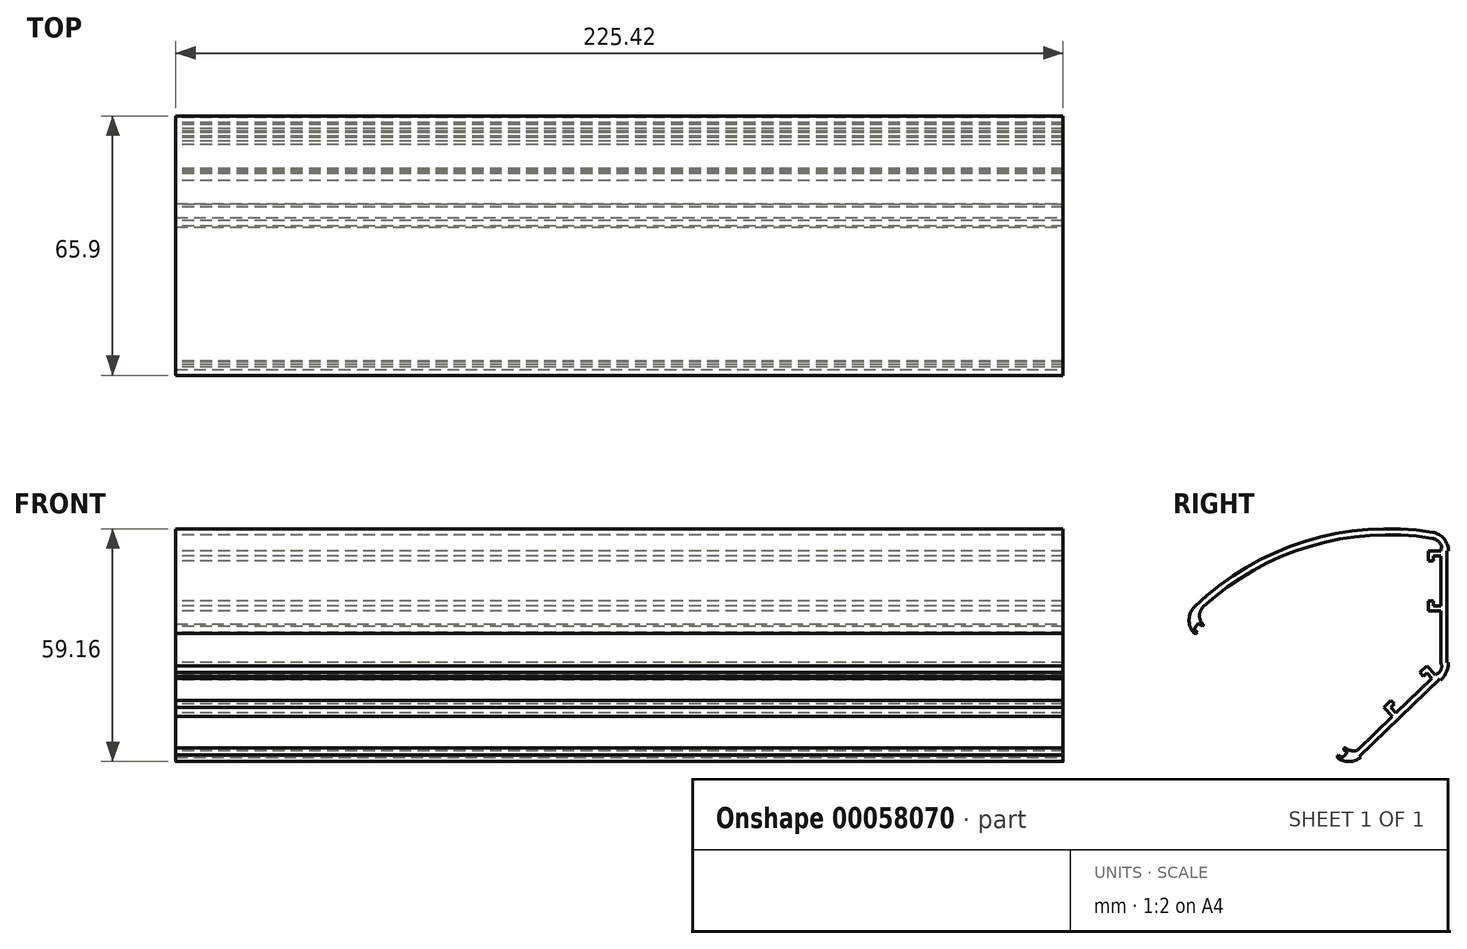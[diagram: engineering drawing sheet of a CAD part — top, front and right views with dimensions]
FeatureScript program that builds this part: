
annotation { "Feature Type Name" : "Feature", "Feature Type Description" : "" }
export const myFeature = defineFeature(function(context is Context, id is Id, definition is map)
    precondition{}
    {
        {
            var Q0;
            Q0=qCreatedBy(makeId("Right.planeOp"),FACE);
            var sketch = newSketch(context, id + "F0", { "sketchPlane" : qUnion([Q0])});
            skLineSegment(sketch, "E0", {"start": v(-25.12, -24.26) * mm, "end": v(0, 0) * mm});
            skLineSegment(sketch, "E1", {"start": v(0, 0) * mm, "end": v(0, 34.93) * mm});
            skArc(sketch, "E2", {"start": v(0, 34.92) * mm, "mid": v(-34.7, 33.87) * mm, "end": v(-64.76, 16.49) * mm});
            skLineSegment(sketch, "E3", {"start": v(-64.76, 16.49) * mm, "end": v(-68.18, 13.16) * mm});
            skLineSegment(sketch, "E4", {"start": v(-25.12, -24.26) * mm, "end": v(-68.18, 13.16) * mm});
            skLineSegment(sketch, "E5", {"start": v(-64.76, 16.49) * mm, "end": v(-25.12, -24.26) * mm, "construction": true});
            skLineSegment(sketch, "E6", {"start": v(-64.76, 16.49) * mm, "end": v(0, 34.93) * mm, "construction": true});
            skSolve(sketch);
        }
        {
            var Q0;
            Q0=qSketchRegion(id+"F0",true);
            extrude(context, id + "F1", {"entities" : qUnion([Q0]), "endBound" : BoundingType.SYMMETRIC, "depth" : 225.42 * mm});
        }
        {
            var Q0;
            Q0=makeQuery(id+"F1.opExtrude","SWEPT_EDGE",EDGE,{"disambiguationData":[OSD([sQuery(id+"F0.wireOp",EDGE,"E1"),sQuery(id+"F0.wireOp",EDGE,"E2")])]});
            var Q1;
            Q1=makeQuery(id+"F1.opExtrude","SWEPT_EDGE",EDGE,{"disambiguationData":[OSD([sQuery(id+"F0.wireOp",EDGE,"E0"),sQuery(id+"F0.wireOp",EDGE,"E4")])]});
            var Q2;
            Q2=makeQuery(id+"F1.opExtrude","SWEPT_EDGE",EDGE,{"disambiguationData":[OSD([sQuery(id+"F0.wireOp",EDGE,"E3"),sQuery(id+"F0.wireOp",EDGE,"E4")])]});
            fillet(context, id + "F2", {"entities" : qUnion([Q0, Q1, Q2]), "radius" : 4.76 * mm, "tangentPropagation" : true, "allowEdgeOverflow" : false});
        }
        {
            var Q0;
            Q0=makeQuery(id+"F1.opExtrude","SWEPT_EDGE",EDGE,{"disambiguationData":[OSD([sQuery(id+"F0.wireOp",EDGE,"E0"),sQuery(id+"F0.wireOp",EDGE,"E1")])]});
            fillet(context, id + "F3", {"entities" : qUnion([Q0]), "radius" : 6.35 * mm, "tangentPropagation" : true, "allowEdgeOverflow" : false});
        }
        {
            var Q0;
            Q0=makeQuery(id+"F1.opExtrude","CAP_FACE",FACE,{"disambiguationData":[OSD([sQuery(id+"F0.wireOp",EDGE,"E0"),sQuery(id+"F0.wireOp",EDGE,"E1"),sQuery(id+"F0.wireOp",EDGE,"E2"),sQuery(id+"F0.wireOp",EDGE,"E3"),sQuery(id+"F0.wireOp",EDGE,"E4")])],"isStart":true});
            var Q1;
            Q1=makeQuery(id+"F1.opExtrude","CAP_FACE",FACE,{"disambiguationData":[OSD([sQuery(id+"F0.wireOp",EDGE,"E0"),sQuery(id+"F0.wireOp",EDGE,"E1"),sQuery(id+"F0.wireOp",EDGE,"E2"),sQuery(id+"F0.wireOp",EDGE,"E3"),sQuery(id+"F0.wireOp",EDGE,"E4")])],"isStart":false});
            var Q2;
            Q2=makeQuery(id+"F1.opExtrude","SWEPT_FACE",FACE,{"disambiguationData":[OSD([sQuery(id+"F0.wireOp",EDGE,"E4")])]});
            shell(context, id + "F4", {"entities" : qUnion([Q0, Q1, Q2]), "thickness" : 1.52 * mm});
        }
        {
            var Q0;
            Q0=makeQuery(id+"F1.opExtrude","CAP_FACE",FACE,{"disambiguationData":[OSD([sQuery(id+"F0.wireOp",EDGE,"E0"),sQuery(id+"F0.wireOp",EDGE,"E1"),sQuery(id+"F0.wireOp",EDGE,"E2"),sQuery(id+"F0.wireOp",EDGE,"E3"),sQuery(id+"F0.wireOp",EDGE,"E4")])],"isStart":true});
            var sketch = newSketch(context, id + "F5", { "sketchPlane" : qUnion([Q0])});
            skLineSegment(sketch, "E7", {"start": v(63.27, 10.92) * mm, "end": v(62.18, 12.16) * mm});
            skArc(sketch, "E8.0", {"start": v(63.27, 10.92) * mm, "mid": v(64.38, 13.28) * mm, "end": v(63.39, 15.7) * mm});
            skArc(sketch, "E9", {"start": v(62.18, 12.16) * mm, "mid": v(63.23, 14.47) * mm, "end": v(62.22, 16.8) * mm});
            skSolve(sketch);
        }
        {
            var Q0;
            {var subQ0=sQuery(id+"F0.wireOp",EDGE,"E3");Q0=makeQuery(id+"FXWxfeTe23RxrKB_1.boolean.opBoolean","MERGE",FACE,{"derivedFrom":[makeQuery(id+"F1.opExtrude","CAP_FACE",FACE,{"disambiguationData":[OSD([sQuery(id+"F0.wireOp",EDGE,"E0"),sQuery(id+"F0.wireOp",EDGE,"E1"),sQuery(id+"F0.wireOp",EDGE,"E2"),subQ0,sQuery(id+"F0.wireOp",EDGE,"E4")])],"isStart":true}),makeQuery(id+"FXWxfeTe23RxrKB_1.opExtrude","CAP_FACE",FACE,{"disambiguationData":[OSD([subQ0,sQuery(id+"F5.wireOp",EDGE,"f8929549-29da-4568-b1ae-587f62ae2228.0"),sQuery(id+"F5.wireOp",EDGE,"E7"),sQuery(id+"F5.wireOp",EDGE,"b0cd2a88-d953-423b-8e6f-4eb86873c5e2")])],"isStart":true})]});}
            var sketch = newSketch(context, id + "F6", { "sketchPlane" : qUnion([Q0])});
            skArc(sketch, "E10.0", {"start": v(23.04, -20.13) * mm, "mid": v(25.2, -21.04) * mm, "end": v(27.42, -20.25) * mm});
            skLineSegment(sketch, "E11", {"start": v(27.42, -20.25) * mm, "end": v(26.33, -19) * mm});
            skArc(sketch, "E12", {"start": v(21.75, -18.88) * mm, "mid": v(24.02, -19.83) * mm, "end": v(26.33, -19) * mm});
            skLineSegment(sketch, "E13", {"start": v(26.33, -19) * mm, "end": v(24.2, -20.85) * mm, "construction": true});
            skSolve(sketch);
        }
        {
            var Q0;
            Q0=makeQuery(id+"F5.imprint","IMPRINT",FACE,{"disambiguationData":[TD([[makeQuery(id+"F5.imprint","IMPRINT",EDGE,{"derivedFrom":sQuery(id+"F5.wireOp",EDGE,"E7")}),-1.0]])]});
            var Q1;
            {var subQ0=sQuery(id+"F6.wireOp",EDGE,"E10.0");Q1=makeQuery(id+"F6.imprint","IMPRINT",FACE,{"disambiguationData":[TD([[makeQuery(id+"F6.imprint","IMPRINT",EDGE,{"derivedFrom":subQ0}),1.0]])]});}
            var Q2;
            Q2=makeQuery(id+"F1.opExtrude","CAP_FACE",FACE,{"disambiguationData":[OSD([sQuery(id+"F0.wireOp",EDGE,"E0"),sQuery(id+"F0.wireOp",EDGE,"E1"),sQuery(id+"F0.wireOp",EDGE,"E2"),sQuery(id+"F0.wireOp",EDGE,"E3"),sQuery(id+"F0.wireOp",EDGE,"E4")])],"isStart":false});
            extrude(context, id + "F7", {"entities" : qUnion([Q0, Q1]), "operationType" : NewBodyOperationType.ADD, "endBound" : BoundingType.UP_TO_SURFACE, "oppositeDirection" : true, "endBoundEntityFace" : qUnion([Q2]), "depth" : 25.4 * mm});
        }
        {
            var Q0;
            {var subQ0=sQuery(id+"F0.wireOp",EDGE,"E0");var subQ1=sQuery(id+"F0.wireOp",EDGE,"E2");Q0=makeQuery(id+"F7.boolean.opBoolean","MERGE",FACE,{"derivedFrom":[makeQuery(id+"F1.opExtrude","CAP_FACE",FACE,{"disambiguationData":[OSD([subQ0,sQuery(id+"F0.wireOp",EDGE,"E1"),subQ1,sQuery(id+"F0.wireOp",EDGE,"E3"),sQuery(id+"F0.wireOp",EDGE,"E4")])],"isStart":true}),makeQuery(id+"F7.opExtrude","CAP_FACE",FACE,{"disambiguationData":[OSD([subQ1,sQuery(id+"F5.wireOp",EDGE,"E7"),sQuery(id+"F5.wireOp",EDGE,"E8.0"),sQuery(id+"F5.wireOp",EDGE,"E9")])],"isStart":true}),makeQuery(id+"F7.opExtrude","CAP_FACE",FACE,{"disambiguationData":[OSD([subQ0,sQuery(id+"F6.wireOp",EDGE,"E10.0"),sQuery(id+"F6.wireOp",EDGE,"E11"),sQuery(id+"F6.wireOp",EDGE,"E12")])],"isStart":true})]});}
            var sketch = newSketch(context, id + "F8", { "sketchPlane" : qUnion([Q0])});
            skLineSegment(sketch, "E14", {"start": v(63.18, 11.01) * mm, "end": v(27.33, -20.15) * mm, "construction": true});
            skSolve(sketch);
        }
        {
            var Q0;
            {var subQ4=sQuery(id+"F0.wireOp",EDGE,"E0");var subQ12=makeQuery(id+"F1.opExtrude","CAP_EDGE",EDGE,{"disambiguationData":[OSD([subQ4])],"isStart":true});Q0=makeQuery(id+"F8.imprint","IMPRINT",FACE,{"disambiguationData":[TD([[makeQuery(id+"F8.imprint","IMPRINT",EDGE,{"derivedFrom":subQ12}),-1.0]])]});}
            var sketch = newSketch(context, id + "F9", { "sketchPlane" : qUnion([Q0])});
            skLineSegment(sketch, "E15", {"start": v(62.56, 11.73) * mm, "end": v(63.8, 10.3) * mm});
            skLineSegment(sketch, "E16", {"start": v(63.8, 10.3) * mm, "end": v(64.77, 11.13) * mm});
            skLineSegment(sketch, "E17", {"start": v(64.77, 11.13) * mm, "end": v(63.52, 12.56) * mm});
            skLineSegment(sketch, "E18", {"start": v(63.52, 12.56) * mm, "end": v(62.56, 11.73) * mm});
            skPoint(sketch, "E19", {"position": v(63.18, 11.01) * mm});
            skSolve(sketch);
        }
        {
            var Q0;
            {var subQ4=sQuery(id+"F0.wireOp",EDGE,"E0");var subQ12=makeQuery(id+"F1.opExtrude","CAP_EDGE",EDGE,{"disambiguationData":[OSD([subQ4])],"isStart":true});Q0=makeQuery(id+"F8.imprint","IMPRINT",FACE,{"disambiguationData":[TD([[makeQuery(id+"F8.imprint","IMPRINT",EDGE,{"derivedFrom":subQ12}),-1.0]])]});}
            var sketch = newSketch(context, id + "F10", { "sketchPlane" : qUnion([Q0])});
            skLineSegment(sketch, "E20", {"start": v(26.7, -19.43) * mm, "end": v(27.96, -20.87) * mm});
            skLineSegment(sketch, "E21", {"start": v(27.96, -20.87) * mm, "end": v(27, -21.7) * mm});
            skLineSegment(sketch, "E22", {"start": v(27, -21.7) * mm, "end": v(25.75, -20.27) * mm});
            skLineSegment(sketch, "E23", {"start": v(25.75, -20.27) * mm, "end": v(26.7, -19.43) * mm});
            skPoint(sketch, "E24", {"position": v(27.33, -20.15) * mm});
            skSolve(sketch);
        }
        {
            var Q0;
            Q0=qSketchRegion(id+"F9",true);
            var Q1;
            Q1=qSketchRegion(id+"F10",true);
            var Q2;
            {var subQ0=sQuery(id+"F0.wireOp",EDGE,"E0");var subQ1=sQuery(id+"F0.wireOp",EDGE,"E2");Q2=makeQuery(id+"F7.boolean.opBoolean","MERGE",FACE,{"derivedFrom":[makeQuery(id+"F1.opExtrude","CAP_FACE",FACE,{"disambiguationData":[OSD([subQ0,sQuery(id+"F0.wireOp",EDGE,"E1"),subQ1,sQuery(id+"F0.wireOp",EDGE,"E3"),sQuery(id+"F0.wireOp",EDGE,"E4")])],"isStart":false}),makeQuery(id+"F7.opExtrude","CAP_FACE",FACE,{"disambiguationData":[OSD([subQ1,sQuery(id+"F5.wireOp",EDGE,"E7"),sQuery(id+"F5.wireOp",EDGE,"E8.0"),sQuery(id+"F5.wireOp",EDGE,"E9")])],"isStart":false}),makeQuery(id+"F7.opExtrude","CAP_FACE",FACE,{"disambiguationData":[OSD([subQ0,sQuery(id+"F6.wireOp",EDGE,"E10.0"),sQuery(id+"F6.wireOp",EDGE,"E11"),sQuery(id+"F6.wireOp",EDGE,"E12")])],"isStart":false})]});}
            extrude(context, id + "F11", {"entities" : qUnion([Q0, Q1]), "operationType" : NewBodyOperationType.REMOVE, "endBound" : BoundingType.UP_TO_SURFACE, "oppositeDirection" : true, "endBoundEntityFace" : qUnion([Q2]), "depth" : 25.4 * mm});
        }
        {
            var Q0;
            Q0=makeQuery(id+"F11.boolean.opBoolean","COPY",EDGE,{"derivedFrom":makeQuery(id+"F11.opExtrude","SWEPT_EDGE",EDGE,{"disambiguationData":[OSD([sQuery(id+"F10.wireOp",EDGE,"E21"),sQuery(id+"F10.wireOp",EDGE,"E22")])]})});
            var Q1;
            Q1=makeQuery(id+"F11.boolean.opBoolean","COPY",EDGE,{"derivedFrom":makeQuery(id+"F11.opExtrude","SWEPT_EDGE",EDGE,{"disambiguationData":[OSD([sQuery(id+"F9.wireOp",EDGE,"E16"),sQuery(id+"F9.wireOp",EDGE,"E17")])]})});
            fillet(context, id + "F12", {"entities" : qUnion([Q0, Q1]), "radius" : 0.76 * mm, "tangentPropagation" : true, "allowEdgeOverflow" : false});
        }
        {
            var Q0;
            {var subQ0=sQuery(id+"F0.wireOp",EDGE,"E4");Q0=makeQuery(id+"F2.opFillet","BLEND_EDGE",EDGE,{"blendedFrom":[makeQuery(id+"F1.opExtrude","SWEPT_EDGE",EDGE,{"disambiguationData":[OSD([sQuery(id+"F0.wireOp",EDGE,"E3"),subQ0])]}),makeQuery(id+"F1.opExtrude","SWEPT_FACE",FACE,{"disambiguationData":[OSD([subQ0])]})],"blendedInto":[makeQuery(id+"F1.opExtrude","SWEPT_FACE",FACE,{"disambiguationData":[OSD([subQ0])]})]});}
            var Q1;
            {var subQ0=sQuery(id+"F0.wireOp",EDGE,"E4");Q1=makeQuery(id+"F2.opFillet","BLEND_EDGE",EDGE,{"blendedFrom":[makeQuery(id+"F1.opExtrude","SWEPT_EDGE",EDGE,{"disambiguationData":[OSD([sQuery(id+"F0.wireOp",EDGE,"E0"),subQ0])]}),makeQuery(id+"F1.opExtrude","SWEPT_FACE",FACE,{"disambiguationData":[OSD([subQ0])]})],"blendedInto":[makeQuery(id+"F1.opExtrude","SWEPT_FACE",FACE,{"disambiguationData":[OSD([subQ0])]})]});}
            fillet(context, id + "F13", {"entities" : qUnion([Q0, Q1]), "radius" : 0.5 * mm, "tangentPropagation" : true, "allowEdgeOverflow" : false});
        }
        {
            var Q0;
            Q0=makeQuery(id+"F11.boolean.opBoolean","COPY",EDGE,{"derivedFrom":makeQuery(id+"F11.opExtrude","SWEPT_EDGE",EDGE,{"disambiguationData":[OSD([sQuery(id+"F10.wireOp",EDGE,"E22"),sQuery(id+"F10.wireOp",EDGE,"E23")])]})});
            var Q1;
            Q1=makeQuery(id+"F11.boolean.opBoolean","COPY",EDGE,{"derivedFrom":makeQuery(id+"F11.opExtrude","SWEPT_EDGE",EDGE,{"disambiguationData":[OSD([sQuery(id+"F0.wireOp",EDGE,"E0"),sQuery(id+"F0.wireOp",EDGE,"E1"),sQuery(id+"F0.wireOp",EDGE,"E2"),sQuery(id+"F0.wireOp",EDGE,"E3"),sQuery(id+"F0.wireOp",EDGE,"E4"),sQuery(id+"F6.wireOp",EDGE,"E11"),sQuery(id+"F10.wireOp",EDGE,"E20"),sQuery(id+"F10.wireOp",EDGE,"E23")])]})});
            var Q2;
            Q2=makeQuery(id+"F7.opExtrude","SWEPT_EDGE",EDGE,{"disambiguationData":[OSD([sQuery(id+"F6.wireOp",EDGE,"E11"),sQuery(id+"F6.wireOp",EDGE,"E12")])]});
            var Q3;
            Q3=makeQuery(id+"F11.boolean.opBoolean","COPY",EDGE,{"derivedFrom":makeQuery(id+"F11.opExtrude","SWEPT_EDGE",EDGE,{"disambiguationData":[OSD([sQuery(id+"F0.wireOp",EDGE,"E0"),sQuery(id+"F0.wireOp",EDGE,"E1"),sQuery(id+"F0.wireOp",EDGE,"E2"),sQuery(id+"F0.wireOp",EDGE,"E3"),sQuery(id+"F0.wireOp",EDGE,"E4"),sQuery(id+"F5.wireOp",EDGE,"E7"),sQuery(id+"F9.wireOp",EDGE,"E15"),sQuery(id+"F9.wireOp",EDGE,"E18")])]})});
            var Q4;
            Q4=makeQuery(id+"F7.opExtrude","SWEPT_EDGE",EDGE,{"disambiguationData":[OSD([sQuery(id+"F5.wireOp",EDGE,"E7"),sQuery(id+"F5.wireOp",EDGE,"E9")])]});
            var Q5;
            Q5=makeQuery(id+"F11.boolean.opBoolean","COPY",EDGE,{"derivedFrom":makeQuery(id+"F11.opExtrude","SWEPT_EDGE",EDGE,{"disambiguationData":[OSD([sQuery(id+"F9.wireOp",EDGE,"E17"),sQuery(id+"F9.wireOp",EDGE,"E18")])]})});
            fillet(context, id + "F14", {"entities" : qUnion([Q0, Q1, Q2, Q3, Q4, Q5]), "radius" : 0.25 * mm, "tangentPropagation" : true, "allowEdgeOverflow" : false});
        }
        {
            var Q0;
            {var subQ2=sQuery(id+"F0.wireOp",EDGE,"E2");var subQ10=makeQuery(id+"F1.opExtrude","CAP_EDGE",EDGE,{"disambiguationData":[OSD([subQ2])],"isStart":true});Q0=makeQuery(id+"F8.imprint","IMPRINT",FACE,{"disambiguationData":[TD([[makeQuery(id+"F8.imprint","IMPRINT",EDGE,{"derivedFrom":subQ10}),-1.0]])]});}
            var sketch = newSketch(context, id + "F15", { "sketchPlane" : qUnion([Q0])});
            skLineSegment(sketch, "E25.0", {"start": v(0, 0) * mm, "end": v(0, 30.99) * mm, "construction": true});
            skLineSegment(sketch, "E25.1", {"start": v(21.98, -21.23) * mm, "end": v(0, 0) * mm, "construction": true});
            skLineSegment(sketch, "E26", {"start": v(0, 0) * mm, "end": v(1.9, 0.8) * mm, "construction": true});
            skSolve(sketch);
        }
        {
            var Q0;
            {var subQ2=sQuery(id+"F0.wireOp",EDGE,"E2");var subQ10=makeQuery(id+"F1.opExtrude","CAP_EDGE",EDGE,{"disambiguationData":[OSD([subQ2])],"isStart":true});Q0=makeQuery(id+"F8.imprint","IMPRINT",FACE,{"disambiguationData":[TD([[makeQuery(id+"F8.imprint","IMPRINT",EDGE,{"derivedFrom":subQ10}),-1.0]])]});}
            var sketch = newSketch(context, id + "F16", { "sketchPlane" : qUnion([Q0])});
            skLineSegment(sketch, "E27.bottom", {"start": v(0, 30.99) * mm, "end": v(0.4, 30.99) * mm});
            skLineSegment(sketch, "E27.top", {"start": v(0, 2.7) * mm, "end": v(0.4, 2.7) * mm});
            skLineSegment(sketch, "E27.left", {"start": v(0, 30.99) * mm, "end": v(0, 2.7) * mm});
            skLineSegment(sketch, "E27.right", {"start": v(0.4, 30.99) * mm, "end": v(0.4, 2.7) * mm});
            skLineSegment(sketch, "E28.MirrorCS", {"start": v(22.56, -21.24) * mm, "end": v(2.21, -1.59) * mm});
            skLineSegment(sketch, "E29.MirrorCS", {"start": v(1.94, -1.87) * mm, "end": v(2.21, -1.59) * mm});
            skLineSegment(sketch, "E30.MirrorCS", {"start": v(22.29, -21.52) * mm, "end": v(1.94, -1.87) * mm});
            skLineSegment(sketch, "E31.MirrorCS", {"start": v(22.29, -21.52) * mm, "end": v(22.56, -21.24) * mm});
            skSolve(sketch);
        }
        {
            var Q0;
            Q0=qSketchRegion(id+"F16",true);
            var Q1;
            {var subQ0=sQuery(id+"F0.wireOp",EDGE,"E0");var subQ1=sQuery(id+"F0.wireOp",EDGE,"E2");Q1=makeQuery(id+"F7.boolean.opBoolean","MERGE",FACE,{"derivedFrom":[makeQuery(id+"F1.opExtrude","CAP_FACE",FACE,{"disambiguationData":[OSD([subQ0,sQuery(id+"F0.wireOp",EDGE,"E1"),subQ1,sQuery(id+"F0.wireOp",EDGE,"E3"),sQuery(id+"F0.wireOp",EDGE,"E4")])],"isStart":false}),makeQuery(id+"F7.opExtrude","CAP_FACE",FACE,{"disambiguationData":[OSD([subQ1,sQuery(id+"F5.wireOp",EDGE,"E7"),sQuery(id+"F5.wireOp",EDGE,"E8.0"),sQuery(id+"F5.wireOp",EDGE,"E9")])],"isStart":false}),makeQuery(id+"F7.opExtrude","CAP_FACE",FACE,{"disambiguationData":[OSD([subQ0,sQuery(id+"F6.wireOp",EDGE,"E10.0"),sQuery(id+"F6.wireOp",EDGE,"E11"),sQuery(id+"F6.wireOp",EDGE,"E12")])],"isStart":false})]});}
            extrude(context, id + "F17", {"entities" : qUnion([Q0]), "operationType" : NewBodyOperationType.REMOVE, "endBound" : BoundingType.UP_TO_SURFACE, "oppositeDirection" : true, "endBoundEntityFace" : qUnion([Q1]), "depth" : 25.4 * mm});
        }
        {
            var Q0;
            {var subQ2=sQuery(id+"F0.wireOp",EDGE,"E2");var subQ10=makeQuery(id+"F1.opExtrude","CAP_EDGE",EDGE,{"disambiguationData":[OSD([subQ2])],"isStart":true});Q0=makeQuery(id+"F8.imprint","IMPRINT",FACE,{"disambiguationData":[TD([[makeQuery(id+"F8.imprint","IMPRINT",EDGE,{"derivedFrom":subQ10}),-1.0]])]});}
            var sketch = newSketch(context, id + "F18", { "sketchPlane" : qUnion([Q0])});
            skLineSegment(sketch, "E32.left", {"start": v(1.52, 30.99) * mm, "end": v(1.52, 2.7) * mm});
            skLineSegment(sketch, "E32.right", {"start": v(1.92, 30.99) * mm, "end": v(1.92, 2.7) * mm});
            skArc(sketch, "E33", {"start": v(1.92, 30.99) * mm, "mid": v(1.88, 31.4) * mm, "end": v(1.76, 31.78) * mm});
            skArc(sketch, "E34", {"start": v(1.76, 31.78) * mm, "mid": v(1.71, 31.98) * mm, "end": v(1.75, 32.18) * mm});
            skArc(sketch, "E35", {"start": v(1.52, 30.99) * mm, "mid": v(1.58, 31.6) * mm, "end": v(1.75, 32.18) * mm});
            skArc(sketch, "E36", {"start": v(1.52, 2.7) * mm, "mid": v(1.56, 2.1) * mm, "end": v(1.67, 1.5) * mm});
            skArc(sketch, "E37", {"start": v(1.92, 2.7) * mm, "mid": v(1.87, 2.29) * mm, "end": v(1.72, 1.9) * mm});
            skArc(sketch, "E38", {"start": v(1.72, 1.9) * mm, "mid": v(1.66, 1.7) * mm, "end": v(1.67, 1.5) * mm});
            skLineSegment(sketch, "E39.MirrorCS", {"start": v(23.62, -20.14) * mm, "end": v(3.27, -0.5) * mm});
            skArc(sketch, "E40.MirrorCS", {"start": v(3.27, -0.5) * mm, "mid": v(2.94, -0.24) * mm, "end": v(2.56, -0.08) * mm});
            skArc(sketch, "E41.MirrorCS", {"start": v(2.56, -0.08) * mm, "mid": v(2.38, 0) * mm, "end": v(2.24, 0.16) * mm});
            skArc(sketch, "E42.MirrorCS", {"start": v(3, -0.78) * mm, "mid": v(2.6, -0.33) * mm, "end": v(2.24, 0.16) * mm});
            skLineSegment(sketch, "E43.MirrorCS", {"start": v(23.35, -20.43) * mm, "end": v(3, -0.78) * mm});
            skArc(sketch, "E44.MirrorCS", {"start": v(23.62, -20.14) * mm, "mid": v(23.89, -20.45) * mm, "end": v(24.08, -20.81) * mm});
            skArc(sketch, "E45.MirrorCS", {"start": v(24.08, -20.81) * mm, "mid": v(24.2, -20.98) * mm, "end": v(24.36, -21.1) * mm});
            skArc(sketch, "E46.MirrorCS", {"start": v(23.35, -20.43) * mm, "mid": v(23.82, -20.8) * mm, "end": v(24.36, -21.1) * mm});
            skSolve(sketch);
        }
        {
            var Q0;
            Q0=qSketchRegion(id+"F18",true);
            var Q1;
            {var subQ0=sQuery(id+"F0.wireOp",EDGE,"E0");var subQ1=sQuery(id+"F0.wireOp",EDGE,"E2");Q1=makeQuery(id+"F7.boolean.opBoolean","MERGE",FACE,{"derivedFrom":[makeQuery(id+"F1.opExtrude","CAP_FACE",FACE,{"disambiguationData":[OSD([subQ0,sQuery(id+"F0.wireOp",EDGE,"E1"),subQ1,sQuery(id+"F0.wireOp",EDGE,"E3"),sQuery(id+"F0.wireOp",EDGE,"E4")])],"isStart":false}),makeQuery(id+"F7.opExtrude","CAP_FACE",FACE,{"disambiguationData":[OSD([subQ1,sQuery(id+"F5.wireOp",EDGE,"E7"),sQuery(id+"F5.wireOp",EDGE,"E8.0"),sQuery(id+"F5.wireOp",EDGE,"E9")])],"isStart":false}),makeQuery(id+"F7.opExtrude","CAP_FACE",FACE,{"disambiguationData":[OSD([subQ0,sQuery(id+"F6.wireOp",EDGE,"E10.0"),sQuery(id+"F6.wireOp",EDGE,"E11"),sQuery(id+"F6.wireOp",EDGE,"E12")])],"isStart":false})]});}
            extrude(context, id + "F19", {"entities" : qUnion([Q0]), "operationType" : NewBodyOperationType.ADD, "endBound" : BoundingType.UP_TO_SURFACE, "oppositeDirection" : true, "endBoundEntityFace" : qUnion([Q1]), "depth" : 25.4 * mm});
        }
        {
            var Q0;
            {var subQ2=sQuery(id+"F0.wireOp",EDGE,"E2");var subQ10=makeQuery(id+"F1.opExtrude","CAP_EDGE",EDGE,{"disambiguationData":[OSD([subQ2])],"isStart":true});Q0=makeQuery(id+"F8.imprint","IMPRINT",FACE,{"disambiguationData":[TD([[makeQuery(id+"F8.imprint","IMPRINT",EDGE,{"derivedFrom":subQ10}),-1.0]])]});}
            var sketch = newSketch(context, id + "F20", { "sketchPlane" : qUnion([Q0])});
            skLineSegment(sketch, "E47", {"start": v(14.24, -11.08) * mm, "end": v(16.44, -8.8) * mm});
            skLineSegment(sketch, "E48", {"start": v(16.44, -8.8) * mm, "end": v(14.61, -7.03) * mm});
            skLineSegment(sketch, "E49", {"start": v(14.61, -7.03) * mm, "end": v(13.73, -7.94) * mm});
            skLineSegment(sketch, "E50", {"start": v(13.73, -7.94) * mm, "end": v(14.65, -8.82) * mm});
            skLineSegment(sketch, "E51", {"start": v(14.65, -8.82) * mm, "end": v(13.32, -10.2) * mm});
            skLineSegment(sketch, "E52", {"start": v(13.32, -10.2) * mm, "end": v(14.24, -11.08) * mm});
            skLineSegment(sketch, "E53", {"start": v(8.75, -5.78) * mm, "end": v(10.96, -3.5) * mm, "construction": true});
            skLineSegment(sketch, "E54.MirrorCS", {"start": v(6.42, -0.88) * mm, "end": v(5.51, 0) * mm});
            skLineSegment(sketch, "E55.MirrorCS", {"start": v(7.3, 0.03) * mm, "end": v(6.42, -0.88) * mm});
            skLineSegment(sketch, "E56.MirrorCS", {"start": v(5.48, 1.8) * mm, "end": v(7.3, 0.03) * mm});
            skLineSegment(sketch, "E57.MirrorCS", {"start": v(3.27, -0.5) * mm, "end": v(5.48, 1.8) * mm});
            skLineSegment(sketch, "E58.MirrorCS", {"start": v(4.19, -1.37) * mm, "end": v(3.27, -0.5) * mm});
            skLineSegment(sketch, "E59.MirrorCS", {"start": v(5.51, 0) * mm, "end": v(4.19, -1.37) * mm});
            skLineSegment(sketch, "E60", {"start": v(1.92, 30.99) * mm, "end": v(5.1, 30.99) * mm});
            skLineSegment(sketch, "E61", {"start": v(5.1, 30.99) * mm, "end": v(5.1, 28.45) * mm});
            skLineSegment(sketch, "E62", {"start": v(5.1, 28.45) * mm, "end": v(3.83, 28.45) * mm});
            skLineSegment(sketch, "E63", {"start": v(3.83, 28.45) * mm, "end": v(3.83, 29.72) * mm});
            skLineSegment(sketch, "E64", {"start": v(3.83, 29.72) * mm, "end": v(1.92, 29.72) * mm});
            skLineSegment(sketch, "E65", {"start": v(1.92, 29.72) * mm, "end": v(1.92, 30.99) * mm});
            skLineSegment(sketch, "E66", {"start": v(1.92, 23.37) * mm, "end": v(5.1, 23.37) * mm, "construction": true});
            skLineSegment(sketch, "E67.MirrorCS", {"start": v(3.83, 18.29) * mm, "end": v(3.83, 17.02) * mm});
            skLineSegment(sketch, "E68.MirrorCS", {"start": v(5.1, 18.29) * mm, "end": v(3.83, 18.29) * mm});
            skLineSegment(sketch, "E69.MirrorCS", {"start": v(5.1, 15.75) * mm, "end": v(5.1, 18.29) * mm});
            skLineSegment(sketch, "E70.MirrorCS", {"start": v(1.92, 15.75) * mm, "end": v(5.1, 15.75) * mm});
            skLineSegment(sketch, "E71.MirrorCS", {"start": v(3.83, 17.02) * mm, "end": v(1.92, 17.02) * mm});
            skLineSegment(sketch, "E72.MirrorCS", {"start": v(1.92, 17.02) * mm, "end": v(1.92, 15.75) * mm});
            skSolve(sketch);
        }
        {
            var Q0;
            Q0=makeQuery(id+"F20.imprint","IMPRINT",FACE,{"disambiguationData":[TD([[makeQuery(id+"F20.imprint","IMPRINT",EDGE,{"derivedFrom":sQuery(id+"F20.wireOp",EDGE,"E60")}),-1.0]])]});
            var Q1;
            Q1=makeQuery(id+"F20.imprint","IMPRINT",FACE,{"disambiguationData":[TD([[makeQuery(id+"F20.imprint","IMPRINT",EDGE,{"derivedFrom":sQuery(id+"F20.wireOp",EDGE,"E67.MirrorCS")}),1.0]])]});
            var Q2;
            Q2=makeQuery(id+"F20.imprint","IMPRINT",FACE,{"disambiguationData":[TD([[makeQuery(id+"F20.imprint","IMPRINT",EDGE,{"derivedFrom":sQuery(id+"F20.wireOp",EDGE,"E54.MirrorCS")}),-1.0]])]});
            var Q3;
            Q3=makeQuery(id+"F20.imprint","IMPRINT",FACE,{"disambiguationData":[TD([[makeQuery(id+"F20.imprint","IMPRINT",EDGE,{"derivedFrom":sQuery(id+"F20.wireOp",EDGE,"E47")}),1.0]])]});
            var Q4;
            {var subQ0=sQuery(id+"F0.wireOp",EDGE,"E0");var subQ1=sQuery(id+"F0.wireOp",EDGE,"E2");Q4=makeQuery(id+"F19.boolean.opBoolean","MERGE",FACE,{"derivedFrom":[makeQuery(id+"F7.boolean.opBoolean","MERGE",FACE,{"derivedFrom":[makeQuery(id+"F1.opExtrude","CAP_FACE",FACE,{"disambiguationData":[OSD([subQ0,sQuery(id+"F0.wireOp",EDGE,"E1"),subQ1,sQuery(id+"F0.wireOp",EDGE,"E3"),sQuery(id+"F0.wireOp",EDGE,"E4")])],"isStart":false}),makeQuery(id+"F7.opExtrude","CAP_FACE",FACE,{"disambiguationData":[OSD([subQ1,sQuery(id+"F5.wireOp",EDGE,"E7"),sQuery(id+"F5.wireOp",EDGE,"E8.0"),sQuery(id+"F5.wireOp",EDGE,"E9")])],"isStart":false}),makeQuery(id+"F7.opExtrude","CAP_FACE",FACE,{"disambiguationData":[OSD([subQ0,sQuery(id+"F6.wireOp",EDGE,"E10.0"),sQuery(id+"F6.wireOp",EDGE,"E11"),sQuery(id+"F6.wireOp",EDGE,"E12")])],"isStart":false})]}),makeQuery(id+"F19.opExtrude","CAP_FACE",FACE,{"disambiguationData":[OSD([sQuery(id+"F18.wireOp",EDGE,"E32.left"),sQuery(id+"F18.wireOp",EDGE,"E32.right"),sQuery(id+"F18.wireOp",EDGE,"E33"),sQuery(id+"F18.wireOp",EDGE,"E34"),sQuery(id+"F18.wireOp",EDGE,"E35"),sQuery(id+"F18.wireOp",EDGE,"E36"),sQuery(id+"F18.wireOp",EDGE,"E37"),sQuery(id+"F18.wireOp",EDGE,"E38")])],"isStart":false}),makeQuery(id+"F19.opExtrude","CAP_FACE",FACE,{"disambiguationData":[OSD([sQuery(id+"F18.wireOp",EDGE,"E39.MirrorCS"),sQuery(id+"F18.wireOp",EDGE,"E40.MirrorCS"),sQuery(id+"F18.wireOp",EDGE,"E41.MirrorCS"),sQuery(id+"F18.wireOp",EDGE,"E42.MirrorCS"),sQuery(id+"F18.wireOp",EDGE,"E43.MirrorCS"),sQuery(id+"F18.wireOp",EDGE,"E44.MirrorCS"),sQuery(id+"F18.wireOp",EDGE,"E45.MirrorCS"),sQuery(id+"F18.wireOp",EDGE,"E46.MirrorCS")])],"isStart":false})]});}
            extrude(context, id + "F21", {"entities" : qUnion([Q0, Q1, Q2, Q3]), "operationType" : NewBodyOperationType.ADD, "endBound" : BoundingType.UP_TO_SURFACE, "oppositeDirection" : true, "endBoundEntityFace" : qUnion([Q4]), "depth" : 25.4 * mm});
        }
    });
